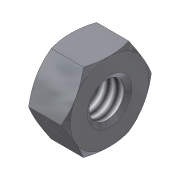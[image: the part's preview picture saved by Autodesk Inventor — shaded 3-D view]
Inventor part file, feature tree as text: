
AUTODESK INVENTOR PART (.ipt)
format: ipt  version: 2016 SP1 (Build 200210100, 210)  size: 148,480 bytes
history: native  units: mm (DEFAULTED — no unit token found)
features: sketch x3, chamfer x1, hole x1
ambient origin geometry x8: Origin, YZ Plane, XZ Plane, XY Plane, X Axis, Y Axis, Z Axis, Center Point
bodies: Solid1 (feature_tree), Body (feature_tree)
feature tree (5):
  chamfer  "Chamfer1"  Angle=30.0deg  [1 undecoded]
  hole  "Thread"  [1 undecoded]
  sketch  "Sketch1"  dims[d0=12.83161mm]
  sketch  "Sketch2"  dims[d1=5.5626mm]
  sketch  "Sketch3"  dims[d2=0.0mm d3=30.0deg d4=30.0deg d5=11.1125mm d6=11.1125mm d7=90.0deg d25=4.9784mm d26=6.0mm d27=4.0mm d28=2.0mm d29=14.3117mm d30=8.0mm d31=20.594885mm d8=0.687408mm d9=30.0deg d10=0.687408mm d11=30.0deg d13=0.0mm d14=0.0mm d39=0.0mm d40=0.687408mm d41=0.687408mm]
note: 2 required parameter values undecoded (feature->parameter linkage not recoverable at this tier; creation-order binding heuristic only, values carry confidence <= 0.55)
